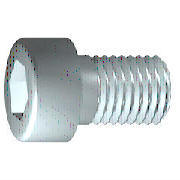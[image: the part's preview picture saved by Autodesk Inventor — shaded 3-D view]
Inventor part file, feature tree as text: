
AUTODESK INVENTOR PART (.ipt)
format: ipt  version: 2025.1 (Build 291241000, 241)  size: 196,096 bytes
history: native  units: mm (DEFAULTED — no unit token found)
features: other x1, extrude x1, plane x1, fillet x1
ambient origin geometry x7: Origin, YZ Plane, XY Plane, X Axis, Y Axis, Z Axis, Center Point
bodies: Solid1 (feature_tree)
feature tree (4):
  other  "Corps"
  extrude  "Rainure"  Depth=8.75mm
  plane  "Work Plane1"
  fillet  "Fillet2"  Radius=0.306825mm
